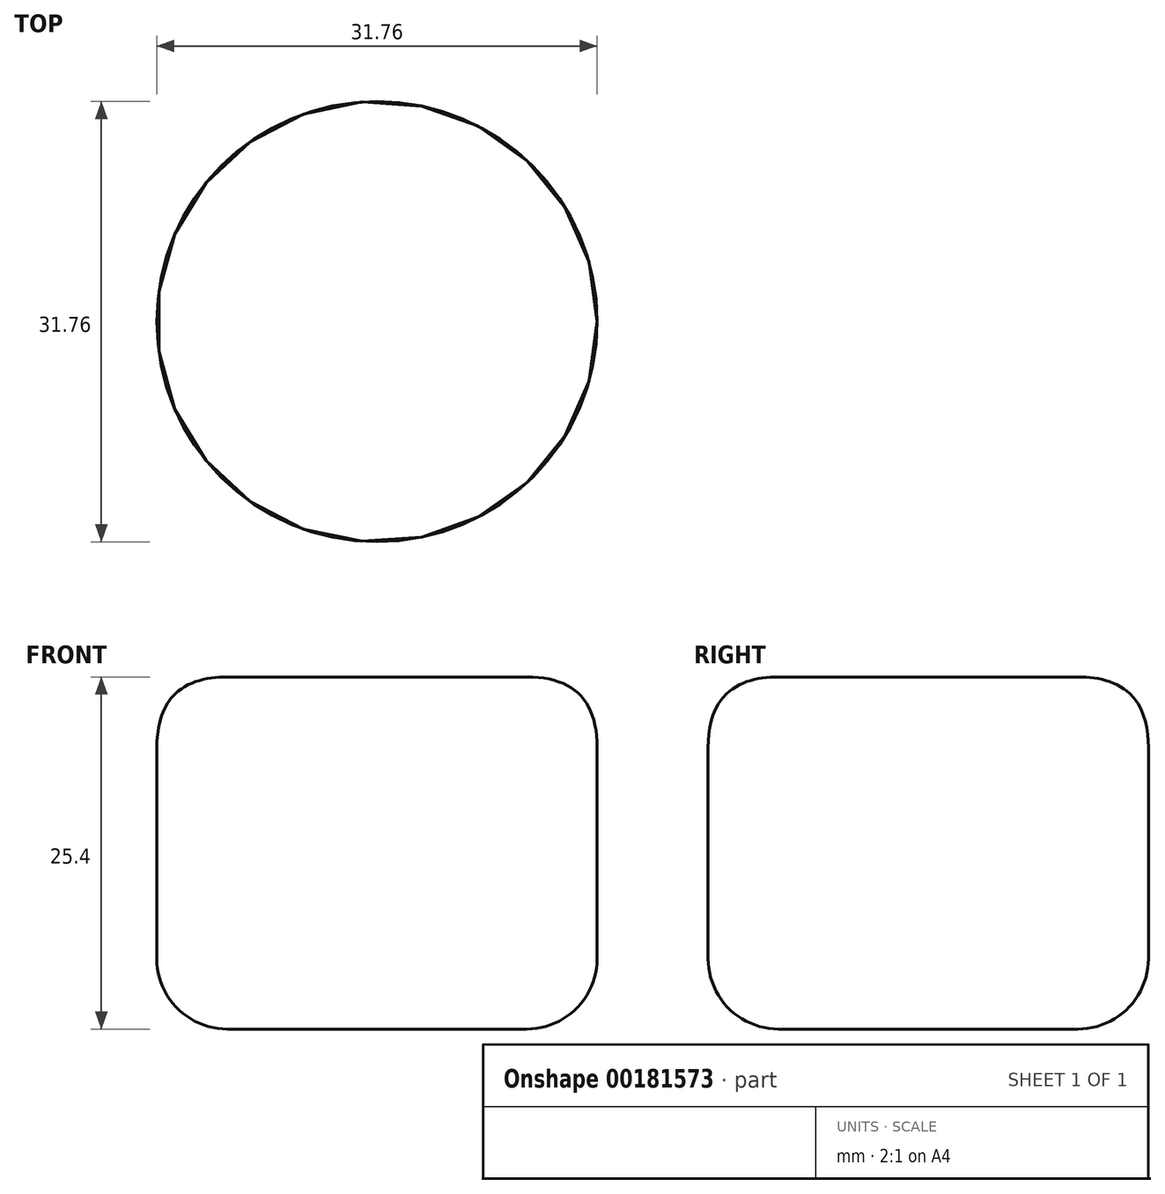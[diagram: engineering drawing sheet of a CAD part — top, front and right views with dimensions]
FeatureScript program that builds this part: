
annotation { "Feature Type Name" : "Feature", "Feature Type Description" : "" }
export const myFeature = defineFeature(function(context is Context, id is Id, definition is map)
    precondition{}
    {
        {
            var Q0;
            Q0=qCreatedBy(makeId("Top.planeOp"),FACE);
            var sketch = newSketch(context, id + "F0", { "sketchPlane" : qUnion([Q0])});
            skCircle(sketch, "E0", {"center": v(0, 0) * mm, "radius": 15.88 * mm});
            skSolve(sketch);
        }
        {
            var Q0;
            Q0 = qSketchRegion(id + "F0", true);
            extrude(context, id + "F1", {"entities" : qUnion([Q0]), "endBound" : BoundingType.SYMMETRIC, "depth" : 25.4 * mm});
        }
        {
            var Q0;
            Q0=makeQuery(id+"F1.opExtrude","CAP_EDGE",EDGE,{"disambiguationData":[OSD([sQuery(id+"F0.wireOp",EDGE,"E0")])],"isStart":false});
            fillet(context, id + "F2", {"entities" : qUnion([Q0]), "radius" : 5.08 * mm, "tangentPropagation" : true, "rho" : 0.5, "crossSection" : FilletCrossSection.CONIC, "allowEdgeOverflow" : false});
        }
        {
            var Q0;
            Q0=makeQuery(id+"F1.opExtrude","CAP_EDGE",EDGE,{"disambiguationData":[OSD([sQuery(id+"F0.wireOp",EDGE,"E0")])],"isStart":true});
            fillet(context, id + "F3", {"entities" : qUnion([Q0]), "radius" : 5.08 * mm, "tangentPropagation" : true, "allowEdgeOverflow" : false});
        }
    });
